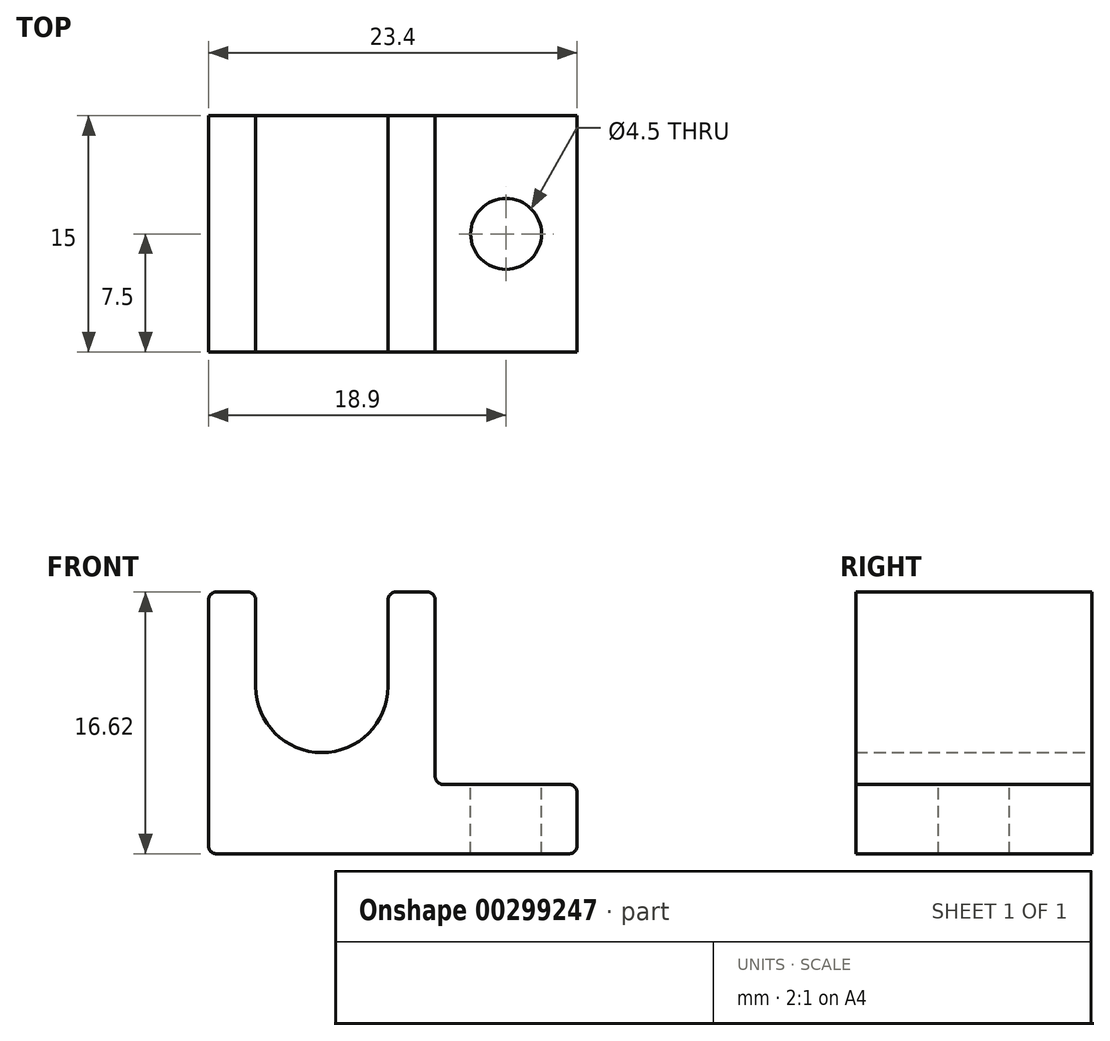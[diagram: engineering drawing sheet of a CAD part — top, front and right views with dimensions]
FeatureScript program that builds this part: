
annotation { "Feature Type Name" : "Feature", "Feature Type Description" : "" }
export const myFeature = defineFeature(function(context is Context, id is Id, definition is map)
    precondition{}
    {
        {
            var Q0;
            Q0=qCreatedBy(makeId("Front.planeOp"),FACE);
            var sketch = newSketch(context, id + "F0", { "sketchPlane" : qUnion([Q0])});
            skArc(sketch, "E0", {"start": v(-4.2, 0) * mm, "mid": v(0, -4.2) * mm, "end": v(4.2, 0) * mm});
            skLineSegment(sketch, "E1", {"start": v(-4.2, 0) * mm, "end": v(-7.2, 0) * mm});
            skLineSegment(sketch, "E2", {"start": v(-7.2, 0) * mm, "end": v(-7.2, -10.62) * mm});
            skLineSegment(sketch, "E3", {"start": v(16.2, -10.62) * mm, "end": v(16.2, -6.22) * mm});
            skLineSegment(sketch, "E4", {"start": v(16.2, -6.22) * mm, "end": v(7.2, -6.22) * mm});
            skLineSegment(sketch, "E5", {"start": v(7.2, -6.22) * mm, "end": v(7.2, 0) * mm});
            skLineSegment(sketch, "E6", {"start": v(7.2, 0) * mm, "end": v(4.2, 0) * mm});
            skPoint(sketch, "E7.start.orphan", {"position": v(0, -10.62) * mm});
            skLineSegment(sketch, "E8", {"start": v(-7.2, -10.62) * mm, "end": v(16.2, -10.62) * mm});
            skSolve(sketch);
        }
        {
            var Q0;
            Q0 = qSketchRegion(id + "F0", true);
            extrude(context, id + "F1", {"entities" : qUnion([Q0]), "depth" : 15 * mm});
        }
        {
            var Q0;
            Q0=makeQuery(id+"F1.opExtrude","SWEPT_FACE",FACE,{"disambiguationData":[OSD([sQuery(id+"F0.wireOp",EDGE,"E1")])]});
            var sketch = newSketch(context, id + "F2", { "sketchPlane" : qUnion([Q0])});
            skLineSegment(sketch, "E9.bottom", {"start": v(-7.2, 0) * mm, "end": v(-4.2, 0) * mm});
            skLineSegment(sketch, "E9.top", {"start": v(-7.2, -15) * mm, "end": v(-4.2, -15) * mm});
            skLineSegment(sketch, "E9.left", {"start": v(-7.2, 0) * mm, "end": v(-7.2, -15) * mm});
            skLineSegment(sketch, "E9.right", {"start": v(-4.2, 0) * mm, "end": v(-4.2, -15) * mm});
            skLineSegment(sketch, "E10.bottom", {"start": v(4.2, 0) * mm, "end": v(7.2, 0) * mm});
            skLineSegment(sketch, "E10.top", {"start": v(4.2, -15) * mm, "end": v(7.2, -15) * mm});
            skLineSegment(sketch, "E10.left", {"start": v(4.2, 0) * mm, "end": v(4.2, -15) * mm});
            skLineSegment(sketch, "E10.right", {"start": v(7.2, 0) * mm, "end": v(7.2, -15) * mm});
            skSolve(sketch);
        }
        {
            var Q0;
            Q0 = qSketchRegion(id + "F2", true);
            extrude(context, id + "F3", {"entities" : qUnion([Q0]), "operationType" : NewBodyOperationType.ADD, "depth" : 6 * mm});
        }
        {
            var Q0;
            Q0=makeQuery(id+"F1.opExtrude","SWEPT_FACE",FACE,{"disambiguationData":[OSD([sQuery(id+"F0.wireOp",EDGE,"E4")])]});
            var sketch = newSketch(context, id + "F4", { "sketchPlane" : qUnion([Q0])});
            skCircle(sketch, "E11", {"center": v(11.7, -7.5) * mm, "radius": 2.25 * mm});
            skPoint(sketch, "E11.centerSnap0", {"position": v(7.2, -7.5) * mm});
            skSolve(sketch);
        }
        {
            var Q0;
            Q0 = qSketchRegion(id + "F4", true);
            extrude(context, id + "F5", {"entities" : qUnion([Q0]), "operationType" : NewBodyOperationType.REMOVE, "oppositeDirection" : true, "depth" : 25 * mm});
        }
        {
            var Q0;
            Q0=makeQuery(id+"F1.opExtrude","SWEPT_EDGE",EDGE,{"disambiguationData":[OSD([sQuery(id+"F0.wireOp",EDGE,"E2"),sQuery(id+"F0.wireOp",EDGE,"E8")])]});
            var Q1;
            Q1=makeQuery(id+"F1.opExtrude","SWEPT_EDGE",EDGE,{"disambiguationData":[OSD([sQuery(id+"F0.wireOp",EDGE,"E3"),sQuery(id+"F0.wireOp",EDGE,"E8")])]});
            var Q2;
            Q2=makeQuery(id+"F3.opExtrude","CAP_EDGE",EDGE,{"disambiguationData":[OSD([sQuery(id+"F2.wireOp",EDGE,"E9.left")])],"isStart":false});
            var Q3;
            Q3=makeQuery(id+"F3.opExtrude","CAP_EDGE",EDGE,{"disambiguationData":[OSD([sQuery(id+"F2.wireOp",EDGE,"E9.right")])],"isStart":false});
            var Q4;
            Q4=makeQuery(id+"F3.opExtrude","CAP_EDGE",EDGE,{"disambiguationData":[OSD([sQuery(id+"F2.wireOp",EDGE,"E10.left")])],"isStart":false});
            var Q5;
            Q5=makeQuery(id+"F3.opExtrude","CAP_EDGE",EDGE,{"disambiguationData":[OSD([sQuery(id+"F2.wireOp",EDGE,"E10.right")])],"isStart":false});
            var Q6;
            Q6=makeQuery(id+"F1.opExtrude","SWEPT_EDGE",EDGE,{"disambiguationData":[OSD([sQuery(id+"F0.wireOp",EDGE,"E4"),sQuery(id+"F0.wireOp",EDGE,"E5")])]});
            fillet(context, id + "F6", {"entities" : qUnion([Q0, Q1, Q2, Q3, Q4, Q5, Q6]), "radius" : 0.5 * mm, "tangentPropagation" : true, "allowEdgeOverflow" : false});
        }
        {
            var Q0;
            Q0=makeQuery(id+"F1.opExtrude","SWEPT_EDGE",EDGE,{"disambiguationData":[OSD([sQuery(id+"F0.wireOp",EDGE,"E3"),sQuery(id+"F0.wireOp",EDGE,"E4")])]});
            fillet(context, id + "F7", {"entities" : qUnion([Q0]), "radius" : 0.5 * mm, "tangentPropagation" : true, "allowEdgeOverflow" : false});
        }
    });
